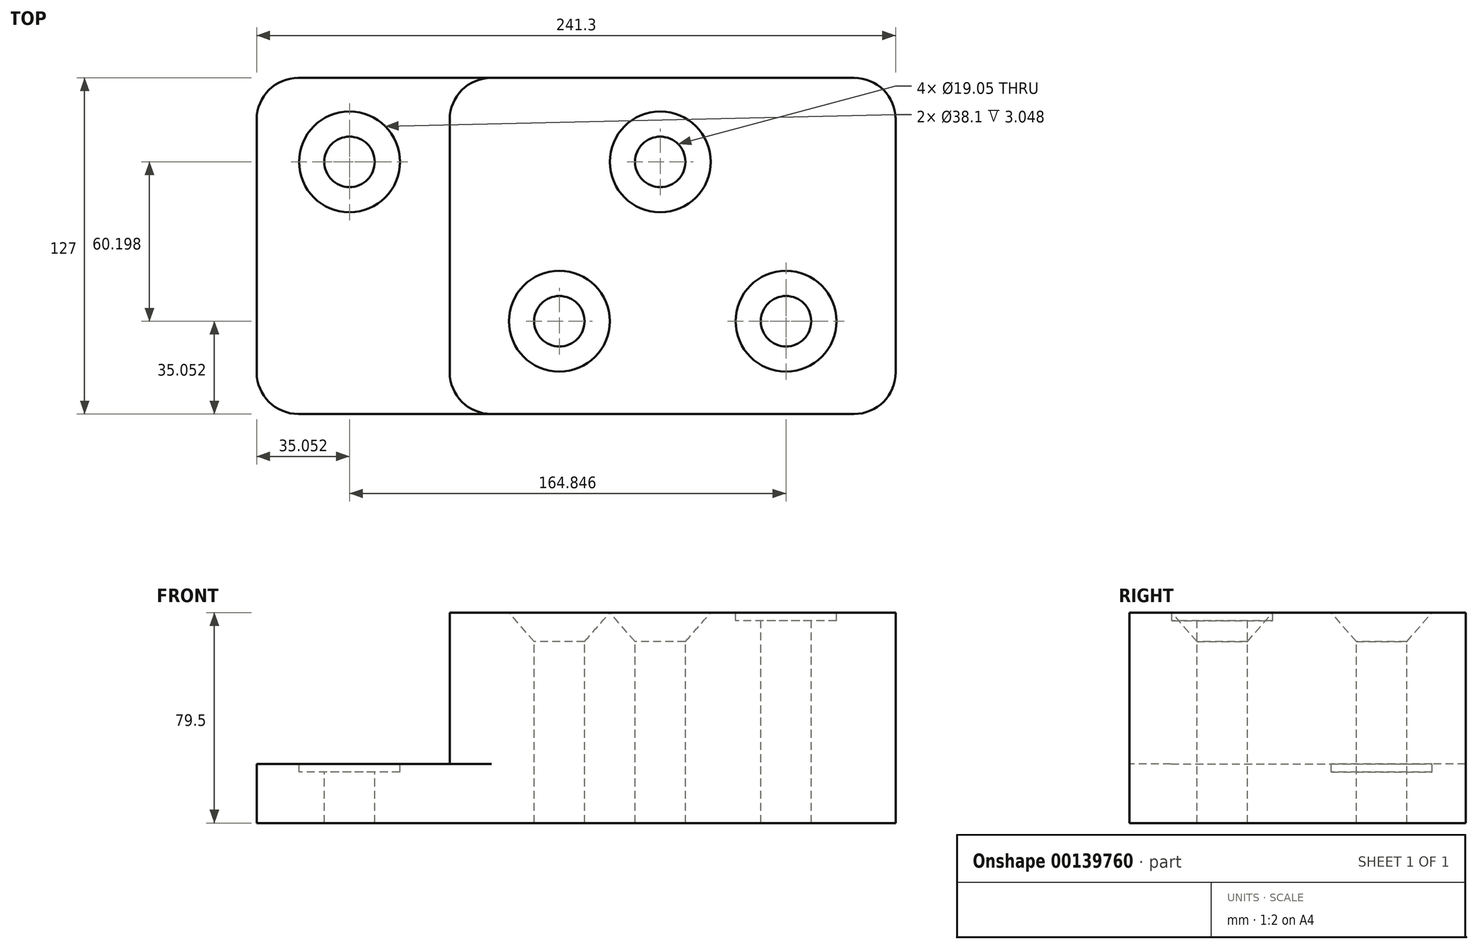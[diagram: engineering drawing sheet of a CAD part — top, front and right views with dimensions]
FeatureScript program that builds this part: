
annotation { "Feature Type Name" : "Feature", "Feature Type Description" : "" }
export const myFeature = defineFeature(function(context is Context, id is Id, definition is map)
    precondition{}
    {
        {
            var Q0;
            Q0=qCreatedBy(makeId("Top.planeOp"),FACE);
            var sketch = newSketch(context, id + "F0", { "sketchPlane" : qUnion([Q0])});
            skLineSegment(sketch, "E0", {"start": v(0, 0) * mm, "end": v(0, 127) * mm});
            skLineSegment(sketch, "E1", {"start": v(0, 127) * mm, "end": v(241.3, 127) * mm});
            skLineSegment(sketch, "E2", {"start": v(241.3, 127) * mm, "end": v(241.3, 0) * mm});
            skLineSegment(sketch, "E3", {"start": v(241.3, 0) * mm, "end": v(0, 0) * mm});
            skSolve(sketch);
        }
        {
            var Q0;
            Q0 = qSketchRegion(id + "F0", true);
            extrude(context, id + "F1", {"entities" : qUnion([Q0]), "depth" : 22.35 * mm});
        }
        {
            var Q0;
            Q0=makeQuery(id+"F1.opExtrude","CAP_FACE",FACE,{"disambiguationData":[OSD([sQuery(id+"F0.wireOp",EDGE,"E0"),sQuery(id+"F0.wireOp",EDGE,"E1"),sQuery(id+"F0.wireOp",EDGE,"E2"),sQuery(id+"F0.wireOp",EDGE,"E3")])],"isStart":false});
            var sketch = newSketch(context, id + "F2", { "sketchPlane" : qUnion([Q0])});
            skLineSegment(sketch, "E4", {"start": v(72.9, 0) * mm, "end": v(72.9, 127) * mm});
            skLineSegment(sketch, "E5", {"start": v(72.9, 127) * mm, "end": v(241.3, 127) * mm});
            skLineSegment(sketch, "E6", {"start": v(241.3, 127) * mm, "end": v(241.3, 0) * mm});
            skLineSegment(sketch, "E7", {"start": v(241.3, 0) * mm, "end": v(72.9, 0) * mm});
            skSolve(sketch);
        }
        {
            var Q0;
            Q0 = qSketchRegion(id + "F2", true);
            extrude(context, id + "F3", {"entities" : qUnion([Q0]), "operationType" : NewBodyOperationType.ADD, "depth" : 57.15 * mm});
        }
        {
            var Q0;
            Q0=makeQuery(id+"F3.boolean.opBoolean","MERGE",EDGE,{"derivedFrom":[makeQuery(id+"F1.opExtrude","SWEPT_EDGE",EDGE,{"disambiguationData":[OSD([sQuery(id+"F0.wireOp",EDGE,"E2"),sQuery(id+"F0.wireOp",EDGE,"E3")])]}),makeQuery(id+"F3.opExtrude","SWEPT_EDGE",EDGE,{"disambiguationData":[OSD([sQuery(id+"F2.wireOp",EDGE,"E6"),sQuery(id+"F2.wireOp",EDGE,"E7")])]})]});
            var Q1;
            Q1=makeQuery(id+"F3.boolean.opBoolean","MERGE",EDGE,{"derivedFrom":[makeQuery(id+"F1.opExtrude","SWEPT_EDGE",EDGE,{"disambiguationData":[OSD([sQuery(id+"F0.wireOp",EDGE,"E1"),sQuery(id+"F0.wireOp",EDGE,"E2")])]}),makeQuery(id+"F3.opExtrude","SWEPT_EDGE",EDGE,{"disambiguationData":[OSD([sQuery(id+"F2.wireOp",EDGE,"E5"),sQuery(id+"F2.wireOp",EDGE,"E6")])]})]});
            var Q2;
            Q2=makeQuery(id+"F3.opExtrude","SWEPT_EDGE",EDGE,{"disambiguationData":[OSD([sQuery(id+"F0.wireOp",EDGE,"E1"),sQuery(id+"F2.wireOp",EDGE,"E4"),sQuery(id+"F2.wireOp",EDGE,"E5")])]});
            var Q3;
            Q3=makeQuery(id+"F3.opExtrude","SWEPT_EDGE",EDGE,{"disambiguationData":[OSD([sQuery(id+"F0.wireOp",EDGE,"E3"),sQuery(id+"F2.wireOp",EDGE,"E4"),sQuery(id+"F2.wireOp",EDGE,"E7")])]});
            var Q4;
            Q4=makeQuery(id+"F1.opExtrude","SWEPT_EDGE",EDGE,{"disambiguationData":[OSD([sQuery(id+"F0.wireOp",EDGE,"E0"),sQuery(id+"F0.wireOp",EDGE,"E3")])]});
            var Q5;
            Q5=makeQuery(id+"F1.opExtrude","SWEPT_EDGE",EDGE,{"disambiguationData":[OSD([sQuery(id+"F0.wireOp",EDGE,"E0"),sQuery(id+"F0.wireOp",EDGE,"E1")])]});
            fillet(context, id + "F4", {"entities" : qUnion([Q0, Q1, Q2, Q3, Q4, Q5]), "radius" : 15.75 * mm, "tangentPropagation" : true, "allowEdgeOverflow" : false});
        }
        {
            var Q0;
            Q0=makeQuery(id+"F3.opExtrude","CAP_FACE",FACE,{"disambiguationData":[OSD([sQuery(id+"F2.wireOp",EDGE,"E4"),sQuery(id+"F2.wireOp",EDGE,"E5"),sQuery(id+"F2.wireOp",EDGE,"E6"),sQuery(id+"F2.wireOp",EDGE,"E7")])],"isStart":false});
            var sketch = newSketch(context, id + "F5", { "sketchPlane" : qUnion([Q0])});
            skPoint(sketch, "E8", {"position": v(199.9, 35.05) * mm});
            skPoint(sketch, "E9", {"position": v(152.4, 95.25) * mm});
            skPoint(sketch, "E10", {"position": v(114.3, 35.05) * mm});
            skSolve(sketch);
        }
        {
            var Q0;
            Q0=makeQuery(id+"F1.opExtrude","CAP_FACE",FACE,{"disambiguationData":[OSD([sQuery(id+"F0.wireOp",EDGE,"E0"),sQuery(id+"F0.wireOp",EDGE,"E1"),sQuery(id+"F0.wireOp",EDGE,"E2"),sQuery(id+"F0.wireOp",EDGE,"E3")])],"isStart":false});
            var sketch = newSketch(context, id + "F6", { "sketchPlane" : qUnion([Q0])});
            skPoint(sketch, "E11", {"position": v(35.05, 95.25) * mm});
            skSolve(sketch);
        }
        {
            var Q0;
            Q0=sQuery(id+"F5.wireOp",VERTEX,"E8");
            var Q1;
            Q1=sQuery(id+"F6.wireOp",VERTEX,"E11");
            var Q2;
            Q2=makeQuery(id+"F1.opExtrude","SWEPT_BODY",BODY,{"disambiguationData":[OSD([sQuery(id+"F0.wireOp",EDGE,"E0"),sQuery(id+"F0.wireOp",EDGE,"E1"),sQuery(id+"F0.wireOp",EDGE,"E2"),sQuery(id+"F0.wireOp",EDGE,"E3")])]});
            hole(context, id + "F7", {"style" : HoleStyle.C_BORE, "endStyle" : HoleEndStyle.THROUGH, "holeDiameter" : 19.05 * mm, "cBoreDiameter" : 38.1 * mm, "cBoreDepth" : 3.05 * mm, "locations" : qUnion([Q0, Q1]), "scope" : qUnion([Q2]), "isTappedThrough" : true});
        }
        {
            var Q0;
            Q0=sQuery(id+"F5.wireOp",VERTEX,"E10");
            var Q1;
            Q1=sQuery(id+"F5.wireOp",VERTEX,"E9");
            var Q2;
            Q2=makeQuery(id+"F1.opExtrude","SWEPT_BODY",BODY,{"disambiguationData":[OSD([sQuery(id+"F0.wireOp",EDGE,"E0"),sQuery(id+"F0.wireOp",EDGE,"E1"),sQuery(id+"F0.wireOp",EDGE,"E2"),sQuery(id+"F0.wireOp",EDGE,"E3")])]});
            hole(context, id + "F8", {"style" : HoleStyle.C_SINK, "endStyle" : HoleEndStyle.THROUGH, "holeDiameter" : 19.05 * mm, "cSinkDiameter" : 38.1 * mm, "cSinkAngle" : 82 * degree, "locations" : qUnion([Q0, Q1]), "scope" : qUnion([Q2]), "isTappedThrough" : true});
        }
    });
